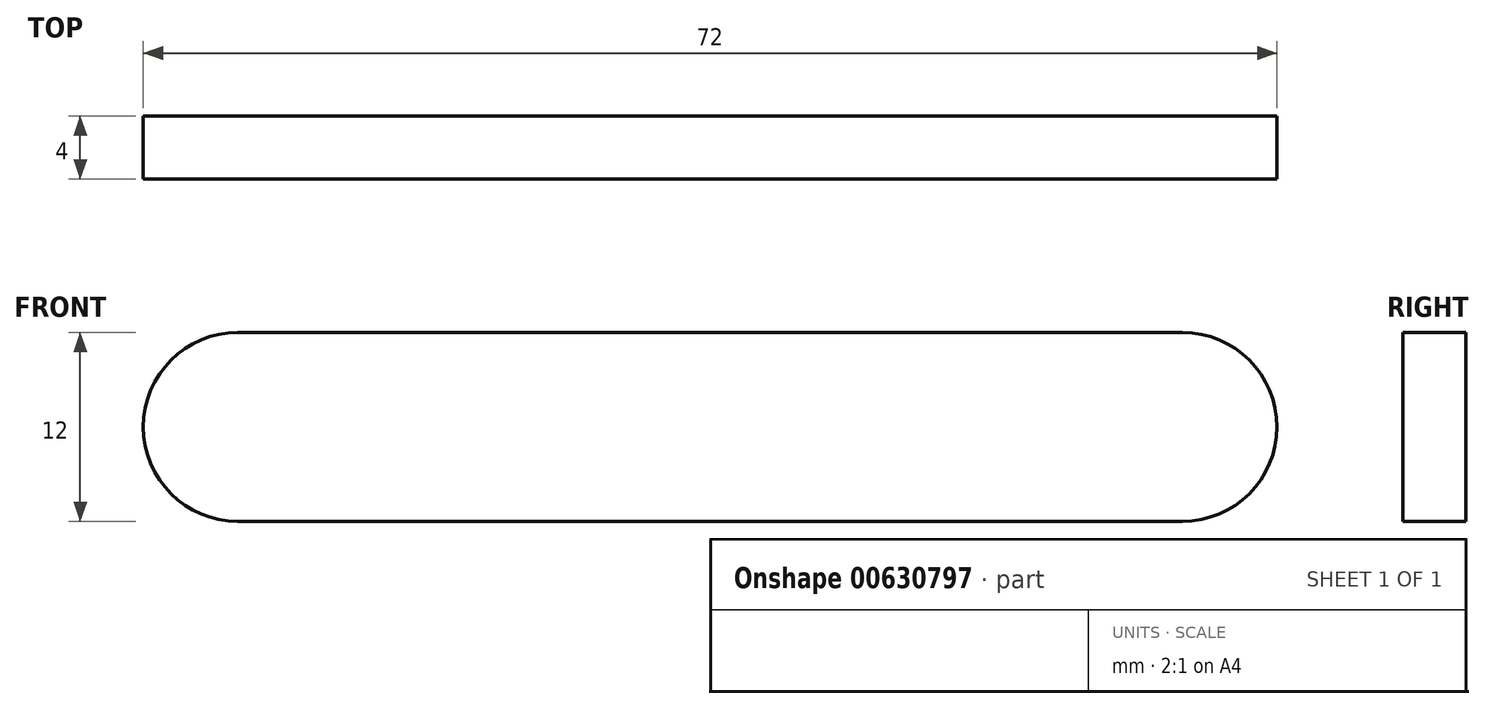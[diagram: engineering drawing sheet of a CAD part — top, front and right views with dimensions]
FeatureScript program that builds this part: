
annotation { "Feature Type Name" : "Feature", "Feature Type Description" : "" }
export const myFeature = defineFeature(function(context is Context, id is Id, definition is map)
    precondition{}
    {
        {
            var Q0;
            Q0=qCreatedBy(makeId("Front.planeOp"),FACE);
            var sketch = newSketch(context, id + "F0", { "sketchPlane" : qUnion([Q0])});
            skLineSegment(sketch, "E0", {"start": v(-28.06, 27.78) * mm, "end": v(31.94, 27.78) * mm});
            skArc(sketch, "E1.0.startCap", {"start": v(-28.06, 21.78) * mm, "mid": v(-34.06, 27.78) * mm, "end": v(-28.06, 33.78) * mm});
            skArc(sketch, "E1.0.endCap", {"start": v(31.94, 33.78) * mm, "mid": v(37.94, 27.78) * mm, "end": v(31.94, 21.78) * mm});
            skLineSegment(sketch, "E1.0.left", {"start": v(-28.06, 33.78) * mm, "end": v(31.94, 33.78) * mm});
            skLineSegment(sketch, "E1.0.right", {"start": v(-28.06, 21.78) * mm, "end": v(31.94, 21.78) * mm});
            skArc(sketch, "E2.0.startCap", {"start": v(-28.06, 20.98) * mm, "mid": v(-34.86, 27.78) * mm, "end": v(-28.06, 34.58) * mm});
            skArc(sketch, "E2.0.endCap", {"start": v(31.94, 34.58) * mm, "mid": v(38.74, 27.78) * mm, "end": v(31.94, 20.98) * mm});
            skLineSegment(sketch, "E2.0.left", {"start": v(-28.06, 34.58) * mm, "end": v(31.94, 34.58) * mm});
            skLineSegment(sketch, "E2.0.right", {"start": v(-28.06, 20.98) * mm, "end": v(31.94, 20.98) * mm});
            skSolve(sketch);
        }
        {
            var Q0;
            Q0=makeQuery(id+"F0.imprint","IMPRINT",FACE,{"disambiguationData":[TD([[makeQuery(id+"F0.imprint","IMPRINT",EDGE,{"derivedFrom":sQuery(id+"F0.wireOp",EDGE,"E1.0.startCap")}),1.0]])]});
            extrude(context, id + "F1", {"entities" : qUnion([Q0]), "depth" : 4 * mm, "offsetDistance" : 25 * mm});
        }
    });
